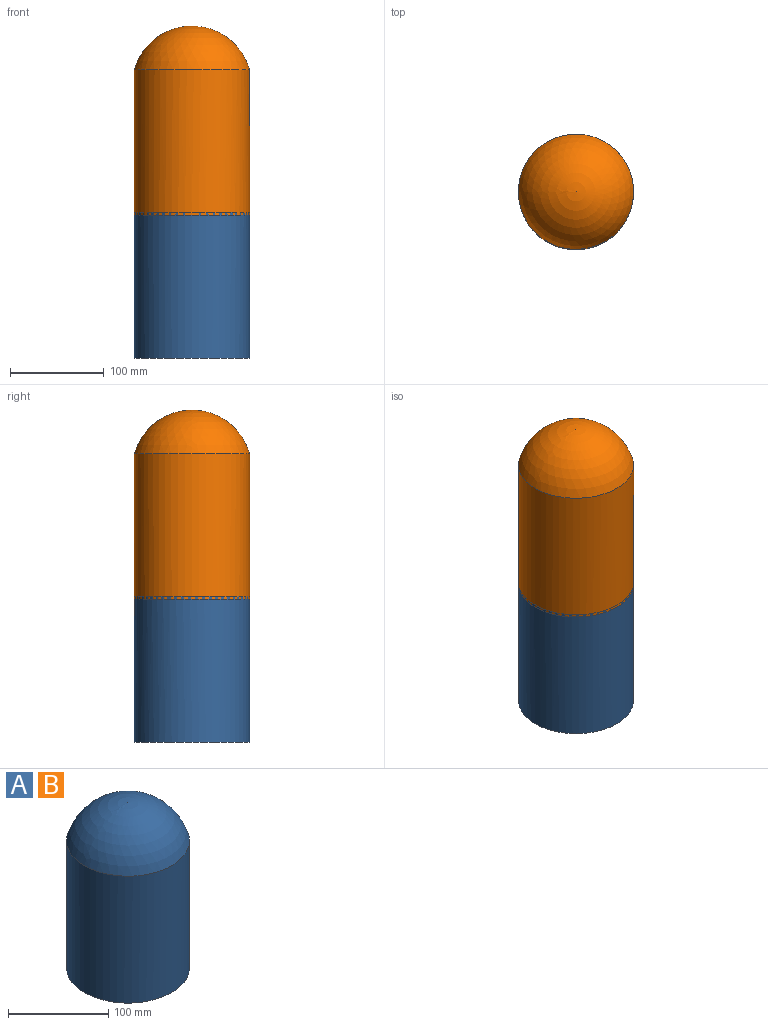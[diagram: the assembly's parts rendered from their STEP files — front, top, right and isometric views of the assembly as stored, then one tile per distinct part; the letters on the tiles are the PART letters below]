
ASSEMBLY  parts=2 mates=1
PART A: 3 faces, bbox 122.9x122.9x201.9 mm
  f0: cylinder r=61.47mm len=155.27mm, axis (0,0,-1), area 59967.3mm2, adj f1,f2
  f1: plane 122.94x122.94mm, normal (0,0,-1), area 11869.9mm2, adj f0
  f2: sphere r=63.82mm, area 18709.8mm2, adj f0
PART B: same geometry as A
PLACE A rot(axis=(0,0,1),90deg) t=(0,0,0)mm
PLACE B rot(axis=(0,0,1),0deg) t=(0,0,152.4)mm
MATE cylindrical B.f0 <-> A.f0  axis (0,0,-1) through (0,0,152.4)mm
